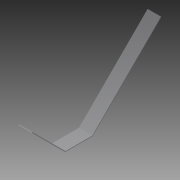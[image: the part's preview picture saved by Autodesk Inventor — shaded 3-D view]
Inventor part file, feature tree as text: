
AUTODESK INVENTOR PART (.ipt)
format: ipt  version: 2014 SP1 (Build 180222100, 222)  size: 104,448 bytes
history: native  units: in
note: dims shown in document units (in); Inventor stores cm internally (conversion verified against a paired STEP export)
features: sketch x3, other x2, extrude x1
ambient origin geometry x8: Origin, YZ Plane, XZ Plane, XY Plane, X Axis, Y Axis, Z Axis, Center Point
bodies: Solid1 (feature_tree)
feature tree (6):
  extrude  "Extrusion1"  Depth=1.0in
  other  "Bend Part1"
  other  "Bend Part2"
  sketch  "Sketch1"  dims[d0=1.0in d1=12.75in]
  sketch  "Sketch2"  dims[d2=0.0625in d3=0.0in]
  sketch  "Sketch4"  dims[d4=5.5in d5=45.0deg d6=0.01in d8=2.0in d9=45.0deg d10=0.01in]
